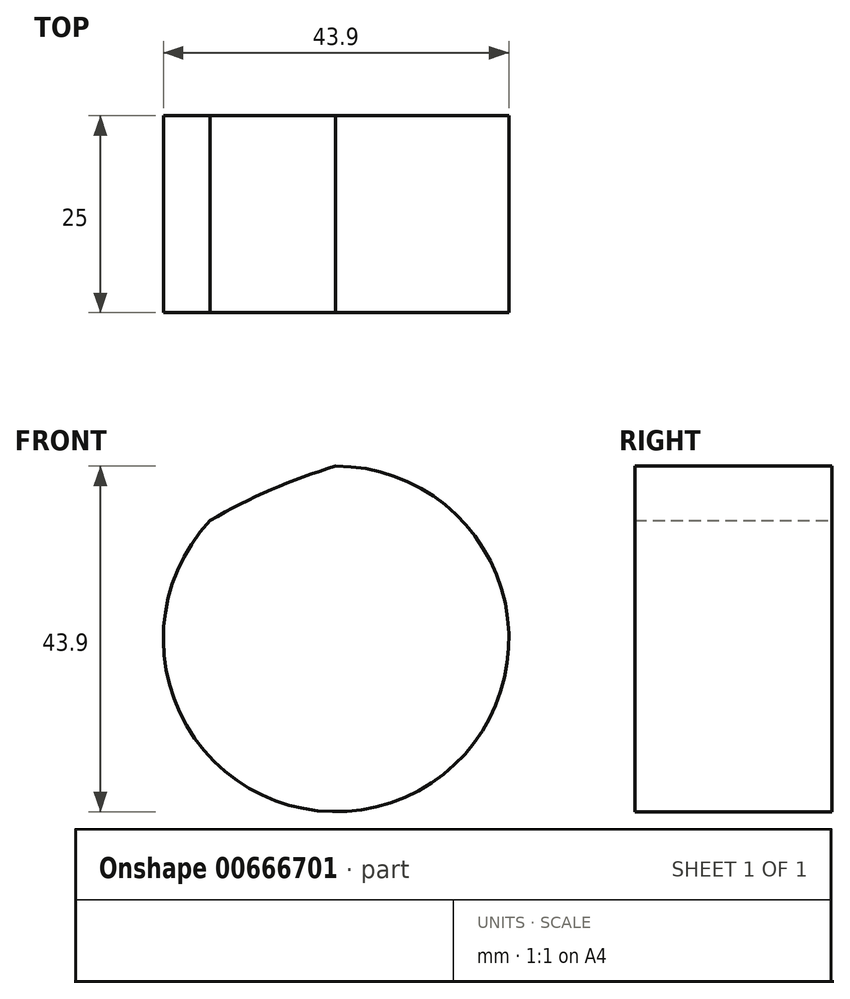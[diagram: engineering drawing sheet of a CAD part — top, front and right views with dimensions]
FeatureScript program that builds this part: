
annotation { "Feature Type Name" : "Feature", "Feature Type Description" : "" }
export const myFeature = defineFeature(function(context is Context, id is Id, definition is map)
    precondition{}
    {
        {
            var Q0;
            Q0=qCreatedBy(makeId("Front.planeOp"),FACE);
            var sketch = newSketch(context, id + "F0", { "sketchPlane" : qUnion([Q0])});
            skCircle(sketch, "E0", {"center": v(0, 0) * mm, "radius": 38.9 * mm});
            skCircle(sketch, "E1", {"center": v(61.7, -2.76) * mm, "radius": 74.18 * mm});
            skCircle(sketch, "E2", {"center": v(40.4, 46.34) * mm, "radius": 21.95 * mm});
            skSolve(sketch);
        }
        {
            var Q0;
            {var subQ0=sQuery(id+"F0.wireOp",EDGE,"E2");var subQ1=sQuery(id+"F0.wireOp",EDGE,"E1");var subQ2=makeQuery(id+"F0.imprint","INTERSECT",VERTEX,{"disambiguationData":[OD(0.0)],"derivedFrom":[subQ1,subQ0]});Q0=makeQuery(id+"F0.imprint","IMPRINT",FACE,{"disambiguationData":[TD([[makeQuery(id+"F0.imprint","IMPRINT",EDGE,{"disambiguationData":[TD([[subQ2,1.0]])],"derivedFrom":subQ1}),1.0]])]});}
            extrude(context, id + "F1", {"entities" : qUnion([Q0]), "depth" : 25 * mm, "offsetDistance" : 25 * mm});
        }
    });
